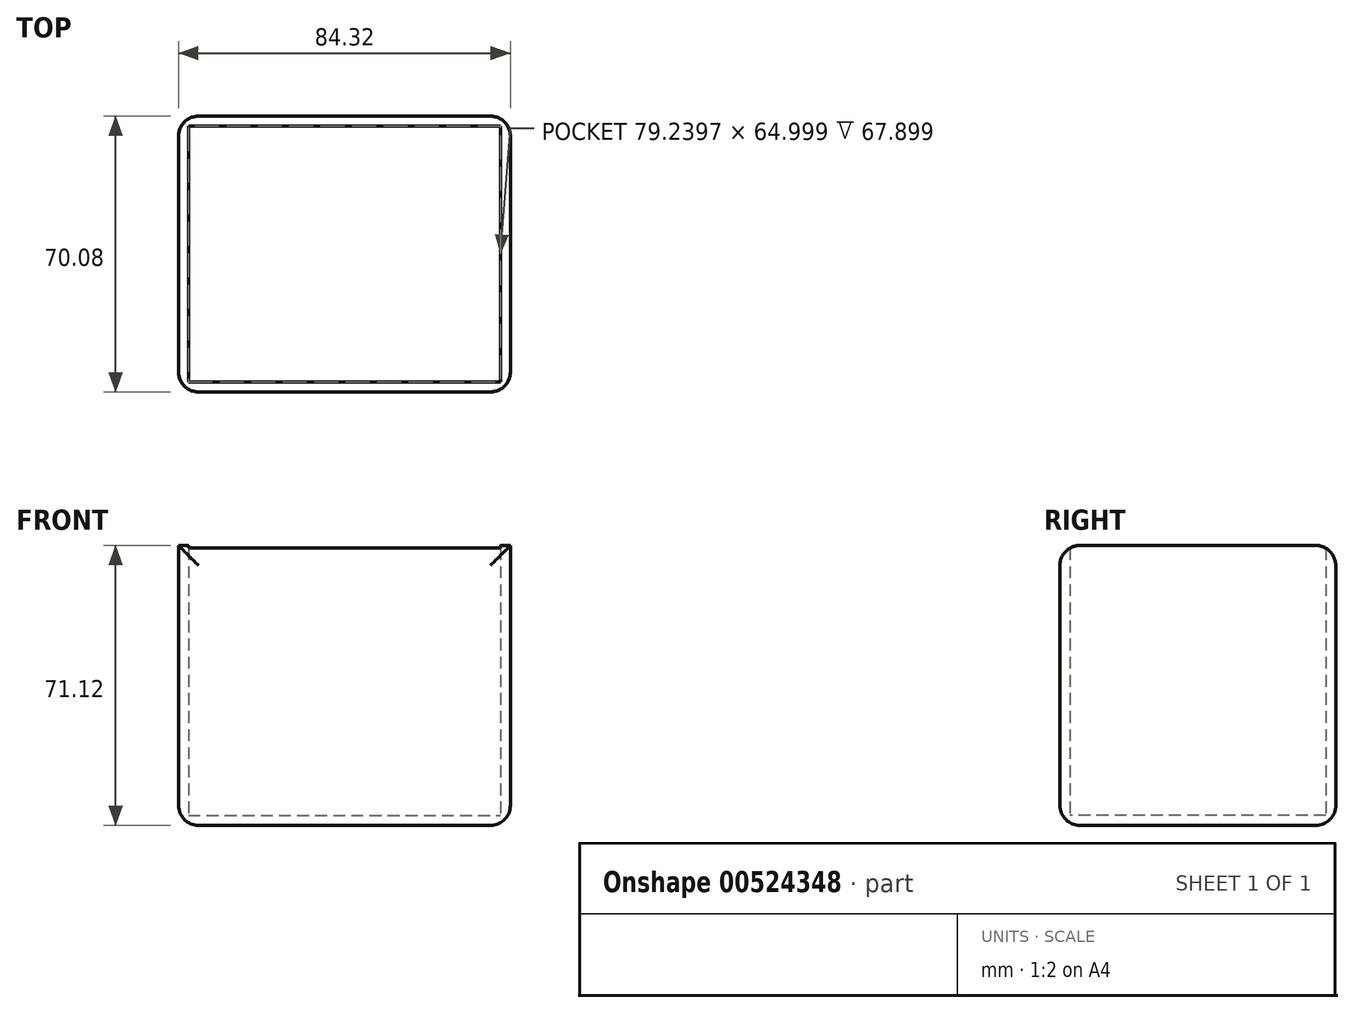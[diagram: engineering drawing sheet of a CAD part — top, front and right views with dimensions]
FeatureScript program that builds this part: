
annotation { "Feature Type Name" : "Feature", "Feature Type Description" : "" }
export const myFeature = defineFeature(function(context is Context, id is Id, definition is map)
    precondition{}
    {
        {
            var Q0;
            Q0=qCreatedBy(makeId("Top.planeOp"),FACE);
            var sketch = newSketch(context, id + "F0", { "sketchPlane" : qUnion([Q0])});
            skLineSegment(sketch, "E0.bottom", {"start": v(-42.72, 30.73) * mm, "end": v(41.6, 30.73) * mm});
            skLineSegment(sketch, "E0.top", {"start": v(-42.72, -39.35) * mm, "end": v(41.6, -39.35) * mm});
            skLineSegment(sketch, "E0.left", {"start": v(-42.72, 30.73) * mm, "end": v(-42.72, -39.35) * mm});
            skLineSegment(sketch, "E0.right", {"start": v(41.6, 30.73) * mm, "end": v(41.6, -39.35) * mm});
            skSolve(sketch);
        }
        {
            var Q0;
            Q0 = qSketchRegion(id + "F0", true);
            extrude(context, id + "F1", {"entities" : qUnion([Q0]), "depth" : 71.12 * mm, "offsetDistance" : 25.4 * mm});
        }
        {
            var Q0;
            Q0=makeQuery(id+"F1.opExtrude","CAP_FACE",FACE,{"disambiguationData":[OSD([sQuery(id+"F0.wireOp",EDGE,"E0.bottom"),sQuery(id+"F0.wireOp",EDGE,"E0.top"),sQuery(id+"F0.wireOp",EDGE,"E0.left"),sQuery(id+"F0.wireOp",EDGE,"E0.right")])],"isStart":false});
            shell(context, id + "F2", {"entities" : qUnion([Q0]), "thickness" : 2.54 * mm});
        }
        {
            var Q0;
            Q0=makeQuery(id+"F1.opExtrude","SWEPT_EDGE",EDGE,{"disambiguationData":[OSD([sQuery(id+"F0.wireOp",EDGE,"E0.top"),sQuery(id+"F0.wireOp",EDGE,"E0.right")])]});
            var Q1;
            Q1=makeQuery(id+"F1.opExtrude","SWEPT_EDGE",EDGE,{"disambiguationData":[OSD([sQuery(id+"F0.wireOp",EDGE,"E0.top"),sQuery(id+"F0.wireOp",EDGE,"E0.left")])]});
            var Q2;
            Q2=makeQuery(id+"F1.opExtrude","CAP_EDGE",EDGE,{"disambiguationData":[OSD([sQuery(id+"F0.wireOp",EDGE,"E0.bottom")])],"isStart":false});
            var Q3;
            Q3=makeQuery(id+"F1.opExtrude","SWEPT_EDGE",EDGE,{"disambiguationData":[OSD([sQuery(id+"F0.wireOp",EDGE,"E0.bottom"),sQuery(id+"F0.wireOp",EDGE,"E0.right")])]});
            var Q4;
            Q4=makeQuery(id+"F1.opExtrude","CAP_EDGE",EDGE,{"disambiguationData":[OSD([sQuery(id+"F0.wireOp",EDGE,"E0.top")])],"isStart":false});
            var Q5;
            Q5=makeQuery(id+"F1.opExtrude","CAP_EDGE",EDGE,{"disambiguationData":[OSD([sQuery(id+"F0.wireOp",EDGE,"E0.bottom")])],"isStart":true});
            var Q6;
            Q6=makeQuery(id+"F1.opExtrude","CAP_EDGE",EDGE,{"disambiguationData":[OSD([sQuery(id+"F0.wireOp",EDGE,"E0.right")])],"isStart":true});
            var Q7;
            Q7=makeQuery(id+"F1.opExtrude","CAP_FACE",FACE,{"disambiguationData":[OSD([sQuery(id+"F0.wireOp",EDGE,"E0.bottom"),sQuery(id+"F0.wireOp",EDGE,"E0.top"),sQuery(id+"F0.wireOp",EDGE,"E0.left"),sQuery(id+"F0.wireOp",EDGE,"E0.right")])],"isStart":true});
            var Q8;
            Q8=makeQuery(id+"F1.opExtrude","SWEPT_EDGE",EDGE,{"disambiguationData":[OSD([sQuery(id+"F0.wireOp",EDGE,"E0.bottom"),sQuery(id+"F0.wireOp",EDGE,"E0.left")])]});
            fillet(context, id + "F3", {"entities" : qUnion([Q0, Q1, Q2, Q3, Q4, Q5, Q6, Q7, Q8]), "radius" : 5.08 * mm, "tangentPropagation" : true, "allowEdgeOverflow" : false});
        }
    });
